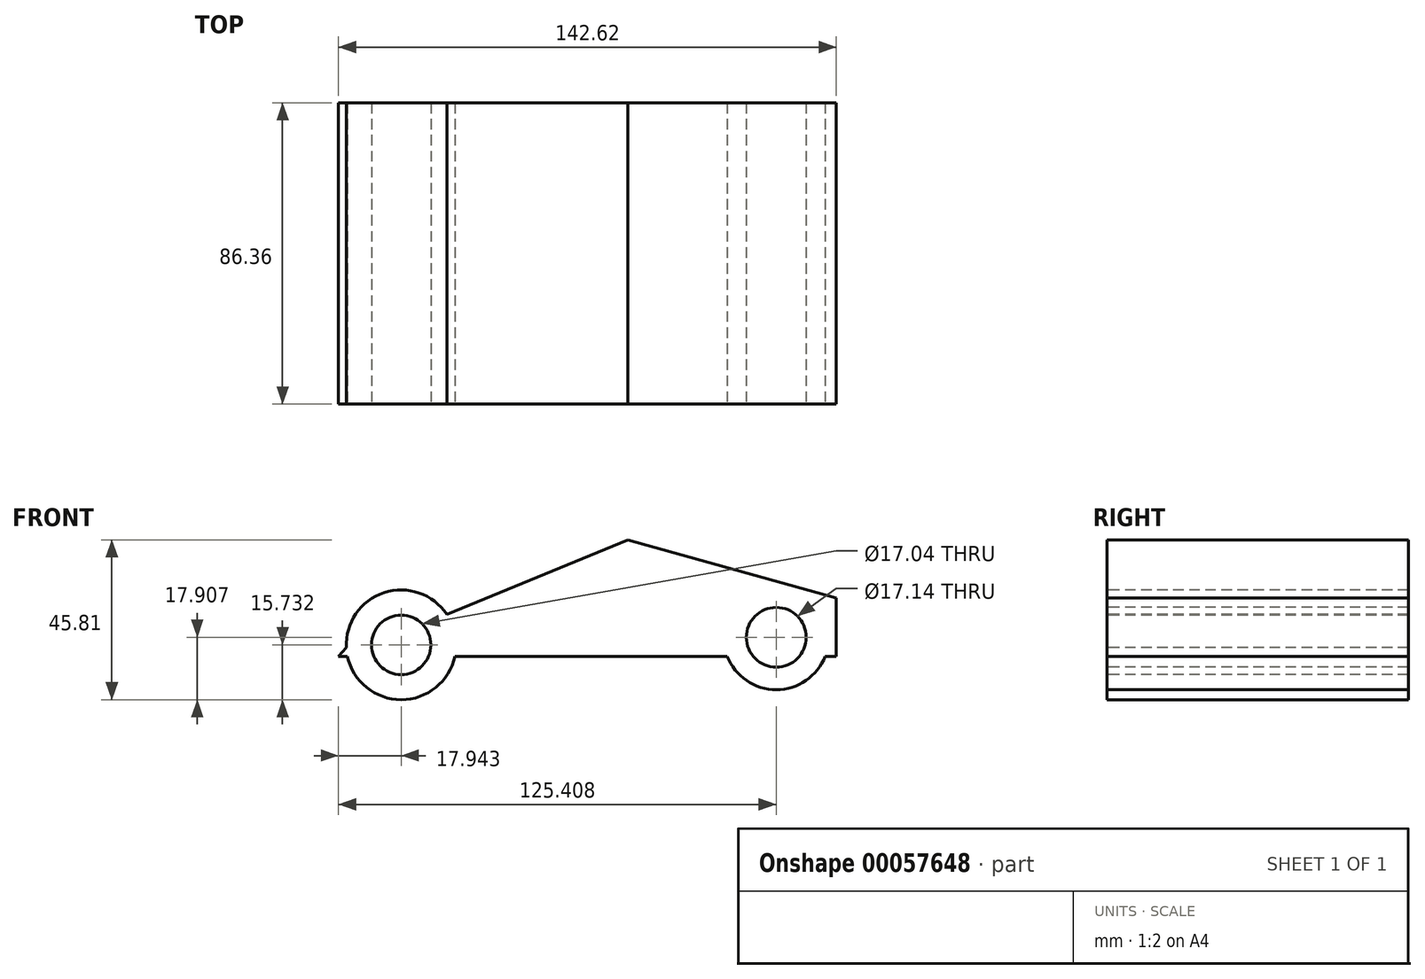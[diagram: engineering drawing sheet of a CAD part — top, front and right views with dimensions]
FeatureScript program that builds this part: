
annotation { "Feature Type Name" : "Feature", "Feature Type Description" : "" }
export const myFeature = defineFeature(function(context is Context, id is Id, definition is map)
    precondition{}
    {
        {
            var Q0;
            Q0=qCreatedBy(makeId("Front.planeOp"),FACE);
            var sketch = newSketch(context, id + "F0", { "sketchPlane" : qUnion([Q0])});
            skLineSegment(sketch, "E0", {"start": v(-72.3, -11.87) * mm, "end": v(70.31, -11.87) * mm});
            skLineSegment(sketch, "E1", {"start": v(70.31, -11.87) * mm, "end": v(70.31, 4.8) * mm});
            skLineSegment(sketch, "E2", {"start": v(70.31, 4.8) * mm, "end": v(10.51, 21.47) * mm});
            skLineSegment(sketch, "E3", {"start": v(10.51, 21.47) * mm, "end": v(-41.68, 0) * mm});
            skLineSegment(sketch, "E4", {"start": v(-41.68, 0) * mm, "end": v(-62.88, -1.36) * mm});
            skLineSegment(sketch, "E5", {"start": v(-62.88, -1.36) * mm, "end": v(-72.3, -11.87) * mm});
            skCircle(sketch, "E6", {"center": v(-54.37, -8.6) * mm, "radius": 15.73 * mm});
            skCircle(sketch, "E7", {"center": v(53.1, -6.43) * mm, "radius": 15.04 * mm});
            skCircle(sketch, "E8", {"center": v(-54.37, -8.6) * mm, "radius": 8.52 * mm});
            skCircle(sketch, "E9", {"center": v(53.1, -6.43) * mm, "radius": 8.57 * mm});
            skSolve(sketch);
        }
        {
            var Q0;
            Q0 = qSketchRegion(id + "F0", true);
            extrude(context, id + "F1", {"entities" : qUnion([Q0]), "oppositeDirection" : true, "depth" : 43.18 * mm});
        }
        {
            var Q0;
            Q0=makeQuery(id+"F1.opExtrude","CAP_FACE",FACE,{"disambiguationData":[OSD([sQuery(id+"F0.wireOp",EDGE,"E0"),sQuery(id+"F0.wireOp",EDGE,"E1"),sQuery(id+"F0.wireOp",EDGE,"E2"),sQuery(id+"F0.wireOp",EDGE,"E3"),sQuery(id+"F0.wireOp",EDGE,"E5"),sQuery(id+"F0.wireOp",EDGE,"E6"),sQuery(id+"F0.wireOp",EDGE,"E7"),sQuery(id+"F0.wireOp",EDGE,"E8"),sQuery(id+"F0.wireOp",EDGE,"E9")])],"isStart":true});
            extrude(context, id + "F2", {"entities" : qUnion([Q0]), "operationType" : NewBodyOperationType.ADD, "depth" : 43.18 * mm});
        }
    });
